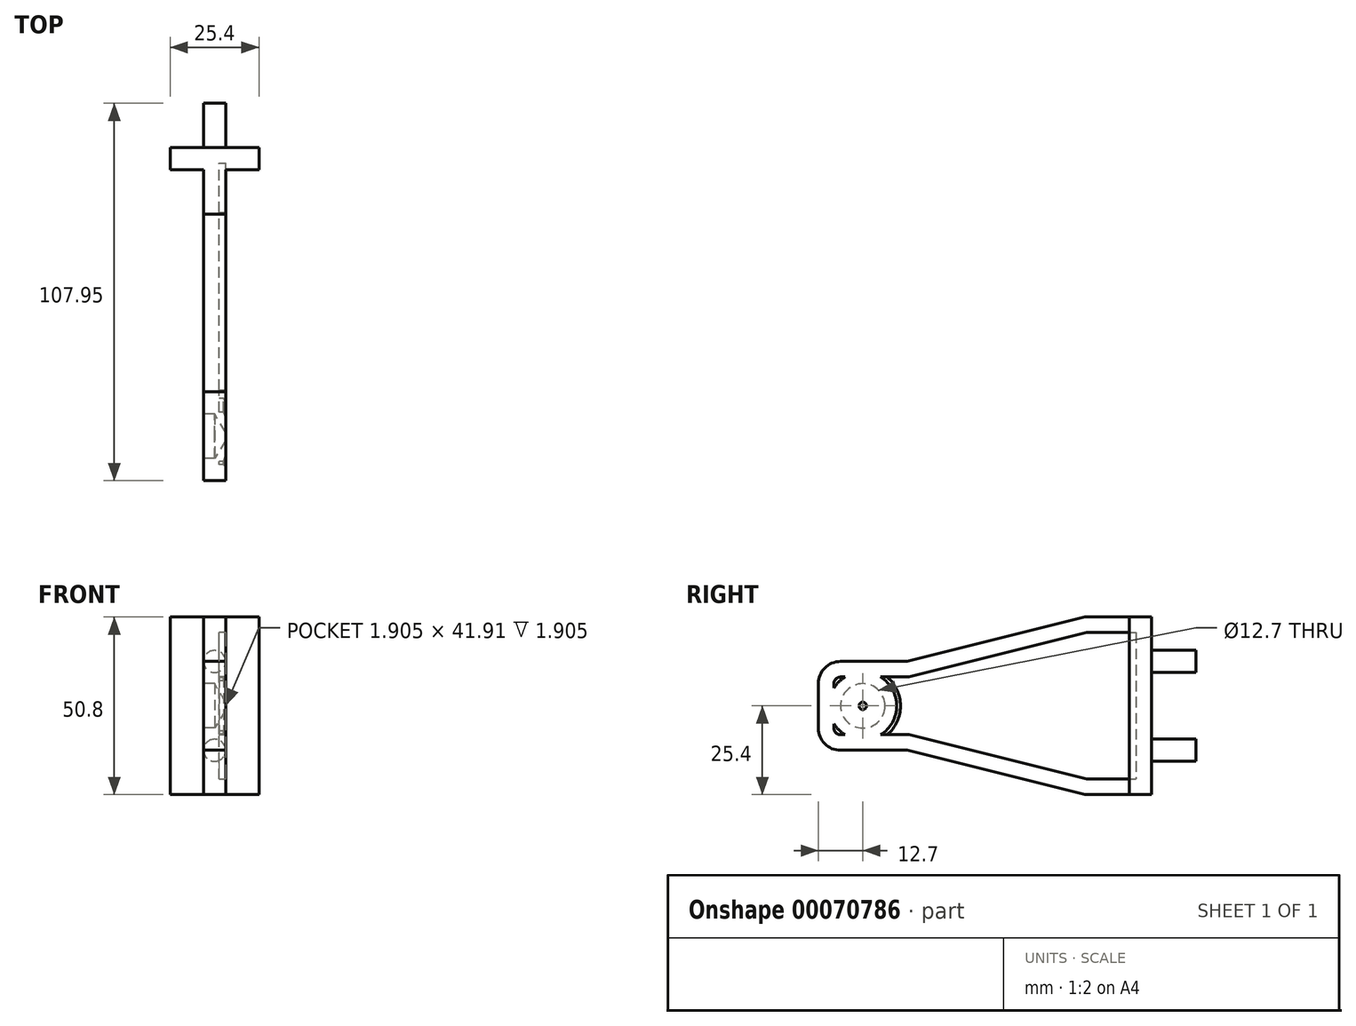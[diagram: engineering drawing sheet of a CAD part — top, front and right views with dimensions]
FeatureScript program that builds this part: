
annotation { "Feature Type Name" : "Feature", "Feature Type Description" : "" }
export const myFeature = defineFeature(function(context is Context, id is Id, definition is map)
    precondition{}
    {
        {
            var Q0;
            Q0=qCreatedBy(makeId("Front.planeOp"),FACE);
            var sketch = newSketch(context, id + "F0", { "sketchPlane" : qUnion([Q0])});
            skLineSegment(sketch, "E0.bottom", {"start": v(0, 0) * mm, "end": v(25.4, 0) * mm});
            skLineSegment(sketch, "E0.top", {"start": v(0, 50.8) * mm, "end": v(25.4, 50.8) * mm});
            skLineSegment(sketch, "E0.left", {"start": v(0, 0) * mm, "end": v(0, 50.8) * mm});
            skLineSegment(sketch, "E0.right", {"start": v(25.4, 0) * mm, "end": v(25.4, 50.8) * mm});
            skSolve(sketch);
        }
        {
            var Q0;
            Q0 = qSketchRegion(id + "F0", true);
            extrude(context, id + "F1", {"entities" : qUnion([Q0]), "depth" : 6.35 * mm});
        }
        {
            var Q0;
            Q0=makeQuery(id+"F1.opExtrude","CAP_FACE",FACE,{"disambiguationData":[OSD([sQuery(id+"F0.wireOp",EDGE,"E0.bottom"),sQuery(id+"F0.wireOp",EDGE,"E0.top"),sQuery(id+"F0.wireOp",EDGE,"E0.left"),sQuery(id+"F0.wireOp",EDGE,"E0.right")])],"isStart":false});
            var sketch = newSketch(context, id + "F2", { "sketchPlane" : qUnion([Q0])});
            skLineSegment(sketch, "E1.bottom", {"start": v(9.53, 0) * mm, "end": v(15.88, 0) * mm});
            skLineSegment(sketch, "E1.top", {"start": v(9.52, 50.8) * mm, "end": v(15.87, 50.8) * mm});
            skLineSegment(sketch, "E1.left", {"start": v(9.53, 0) * mm, "end": v(9.52, 50.8) * mm});
            skLineSegment(sketch, "E1.right", {"start": v(15.88, 0) * mm, "end": v(15.87, 50.8) * mm});
            skSolve(sketch);
        }
        {
            var Q0;
            Q0 = qSketchRegion(id + "F2", true);
            extrude(context, id + "F3", {"entities" : qUnion([Q0]), "operationType" : NewBodyOperationType.ADD, "depth" : 12.7 * mm});
        }
        {
            var Q0;
            Q0=makeQuery(id+"F3.opExtrude","CAP_FACE",FACE,{"disambiguationData":[OSD([sQuery(id+"F2.wireOp",EDGE,"E1.bottom"),sQuery(id+"F2.wireOp",EDGE,"E1.top"),sQuery(id+"F2.wireOp",EDGE,"E1.left"),sQuery(id+"F2.wireOp",EDGE,"E1.right")])],"isStart":false});
            cPlane(context, id + "F4", {"entities" : qUnion([Q0]), "cplaneType" : CPlaneType.OFFSET, "offset" : 50.8 * mm, "width" : 152.4 * mm, "height" : 152.4 * mm});
        }
        {
            var Q0;
            Q0=qCreatedBy(id+"F4.planeOp",FACE);
            var sketch = newSketch(context, id + "F5", { "sketchPlane" : qUnion([Q0])});
            skLineSegment(sketch, "E2.0", {"start": v(9.53, 12.7) * mm, "end": v(9.53, 38.1) * mm});
            skLineSegment(sketch, "E3.0", {"start": v(15.88, 12.7) * mm, "end": v(15.87, 38.1) * mm});
            skLineSegment(sketch, "E4", {"start": v(9.53, 38.1) * mm, "end": v(15.87, 38.1) * mm});
            skLineSegment(sketch, "E5", {"start": v(9.53, 12.7) * mm, "end": v(15.88, 12.7) * mm});
            skSolve(sketch);
        }
        {
            var Q1;
            Q1=makeQuery(id+"F3.opExtrude","CAP_FACE",FACE,{"disambiguationData":[OSD([sQuery(id+"F2.wireOp",EDGE,"E1.bottom"),sQuery(id+"F2.wireOp",EDGE,"E1.top"),sQuery(id+"F2.wireOp",EDGE,"E1.left"),sQuery(id+"F2.wireOp",EDGE,"E1.right")])],"isStart":false});
            var Q2;
            Q2=makeQuery(id+"F5.imprint","IMPRINT",FACE,{"disambiguationData":[TD([[makeQuery(id+"F5.imprint","IMPRINT",EDGE,{"derivedFrom":sQuery(id+"F5.wireOp",EDGE,"E2.0")}),-1.0]])]});
            loft(context, id + "F6", {"operationType" : NewBodyOperationType.ADD, "sheetProfilesArray" : [{ "sheetProfileEntities" : qUnion([Q1]) }, { "sheetProfileEntities" : qUnion([Q2]) }]});
        }
        {
            var Q0;
            Q0=makeQuery(id+"F6.opLoft","CAP_FACE",FACE,{"disambiguationData":[OSD([makeQuery(id+"F5.imprint","IMPRINT",FACE,{"disambiguationData":[TD([[makeQuery(id+"F5.imprint","IMPRINT",EDGE,{"derivedFrom":sQuery(id+"F5.wireOp",EDGE,"E2.0")}),-1.0]])]})])],"isStart":true});
            extrude(context, id + "F7", {"entities" : qUnion([Q0]), "operationType" : NewBodyOperationType.ADD, "depth" : 25.4 * mm});
        }
        {
            var Q0;
            Q0=makeQuery(id+"F7.opExtrude","CAP_EDGE",EDGE,{"disambiguationData":[OSD([sQuery(id+"F5.wireOp",EDGE,"E2.0"),sQuery(id+"F5.wireOp",EDGE,"E3.0"),sQuery(id+"F5.wireOp",EDGE,"E5")])],"isStart":false});
            var Q1;
            Q1=makeQuery(id+"F7.opExtrude","CAP_EDGE",EDGE,{"disambiguationData":[OSD([sQuery(id+"F5.wireOp",EDGE,"E2.0"),sQuery(id+"F5.wireOp",EDGE,"E3.0"),sQuery(id+"F5.wireOp",EDGE,"E4")])],"isStart":false});
            fillet(context, id + "F8", {"entities" : qUnion([Q0, Q1]), "radius" : 6.35 * mm, "tangentPropagation" : true, "allowEdgeOverflow" : false});
        }
        {
            var Q0;
            {var subQ0=sQuery(id+"F5.wireOp",EDGE,"E5");var subQ1=sQuery(id+"F5.wireOp",EDGE,"E4");var subQ2=sQuery(id+"F5.wireOp",EDGE,"E2.0");var subQ3=sQuery(id+"F2.wireOp",EDGE,"E1.left");Q0=makeQuery(id+"F7.boolean.opBoolean","MERGE",FACE,{"derivedFrom":[makeQuery(id+"F6.boolean.opBoolean","MERGE",FACE,{"derivedFrom":[makeQuery(id+"F3.opExtrude","SWEPT_FACE",FACE,{"disambiguationData":[OSD([subQ3])]}),makeQuery(id+"F6.opLoft","SWEPT_FACE",FACE,{"disambiguationData":[OSD([sQuery(id+"F0.wireOp",EDGE,"E0.bottom"),sQuery(id+"F0.wireOp",EDGE,"E0.top"),sQuery(id+"F2.wireOp",EDGE,"E1.bottom"),sQuery(id+"F2.wireOp",EDGE,"E1.top"),subQ3,subQ2,subQ1,subQ0])]})]}),makeQuery(id+"F7.opExtrude","SWEPT_FACE",FACE,{"disambiguationData":[OSD([subQ2,subQ1,subQ0])]})]});}
            var sketch = newSketch(context, id + "F9", { "sketchPlane" : qUnion([Q0])});
            skPoint(sketch, "E6", {"position": v(95.25, 25.4) * mm});
            skPoint(sketch, "E7", {"position": v(82.55, 25.4) * mm});
            skSolve(sketch);
        }
        {
            var Q0;
            Q0=sQuery(id+"F9.wireOp",VERTEX,"E7");
            var Q1;
            Q1=makeQuery(id+"F1.opExtrude","SWEPT_BODY",BODY,{"disambiguationData":[OSD([sQuery(id+"F0.wireOp",EDGE,"E0.bottom"),sQuery(id+"F0.wireOp",EDGE,"E0.top"),sQuery(id+"F0.wireOp",EDGE,"E0.left"),sQuery(id+"F0.wireOp",EDGE,"E0.right")])]});
            hole(context, id + "F10", {"style" : HoleStyle.SIMPLE, "endStyle" : HoleEndStyle.BLIND, "holeDiameter" : 12.7 * mm, "holeDepth" : 3.17 * mm, "locations" : qUnion([Q0]), "scope" : qUnion([Q1])});
        }
        {
            var Q0;
            Q0=makeQuery(id+"F1.opExtrude","CAP_FACE",FACE,{"disambiguationData":[OSD([sQuery(id+"F0.wireOp",EDGE,"E0.bottom"),sQuery(id+"F0.wireOp",EDGE,"E0.top"),sQuery(id+"F0.wireOp",EDGE,"E0.left"),sQuery(id+"F0.wireOp",EDGE,"E0.right")])],"isStart":true});
            var sketch = newSketch(context, id + "F11", { "sketchPlane" : qUnion([Q0])});
            skCircle(sketch, "E8", {"center": v(-12.7, 38.1) * mm, "radius": 3.18 * mm});
            skPoint(sketch, "E8.centerSnap0", {"position": v(-12.7, 50.8) * mm});
            skCircle(sketch, "E9", {"center": v(-12.7, 12.7) * mm, "radius": 3.18 * mm});
            skSolve(sketch);
        }
        {
            var Q0;
            Q0 = qSketchRegion(id + "F11", true);
            extrude(context, id + "F12", {"entities" : qUnion([Q0]), "operationType" : NewBodyOperationType.ADD, "depth" : 12.7 * mm});
        }
        {
            var Q0;
            {var subQ0=sQuery(id+"F5.wireOp",EDGE,"E5");var subQ1=sQuery(id+"F5.wireOp",EDGE,"E4");var subQ2=sQuery(id+"F5.wireOp",EDGE,"E3.0");var subQ3=sQuery(id+"F2.wireOp",EDGE,"E1.right");Q0=makeQuery(id+"F7.boolean.opBoolean","MERGE",FACE,{"derivedFrom":[makeQuery(id+"F6.boolean.opBoolean","MERGE",FACE,{"derivedFrom":[makeQuery(id+"F3.opExtrude","SWEPT_FACE",FACE,{"disambiguationData":[OSD([subQ3])]}),makeQuery(id+"F6.opLoft","SWEPT_FACE",FACE,{"disambiguationData":[OSD([sQuery(id+"F0.wireOp",EDGE,"E0.bottom"),sQuery(id+"F0.wireOp",EDGE,"E0.top"),sQuery(id+"F2.wireOp",EDGE,"E1.bottom"),sQuery(id+"F2.wireOp",EDGE,"E1.top"),subQ3,subQ2,subQ1,subQ0])]})]}),makeQuery(id+"F7.opExtrude","SWEPT_FACE",FACE,{"disambiguationData":[OSD([subQ2,subQ1,subQ0])]})]});}
            shell(context, id + "F13", {"entities" : qUnion([Q0]), "thickness" : 4.44 * mm});
        }
    });
